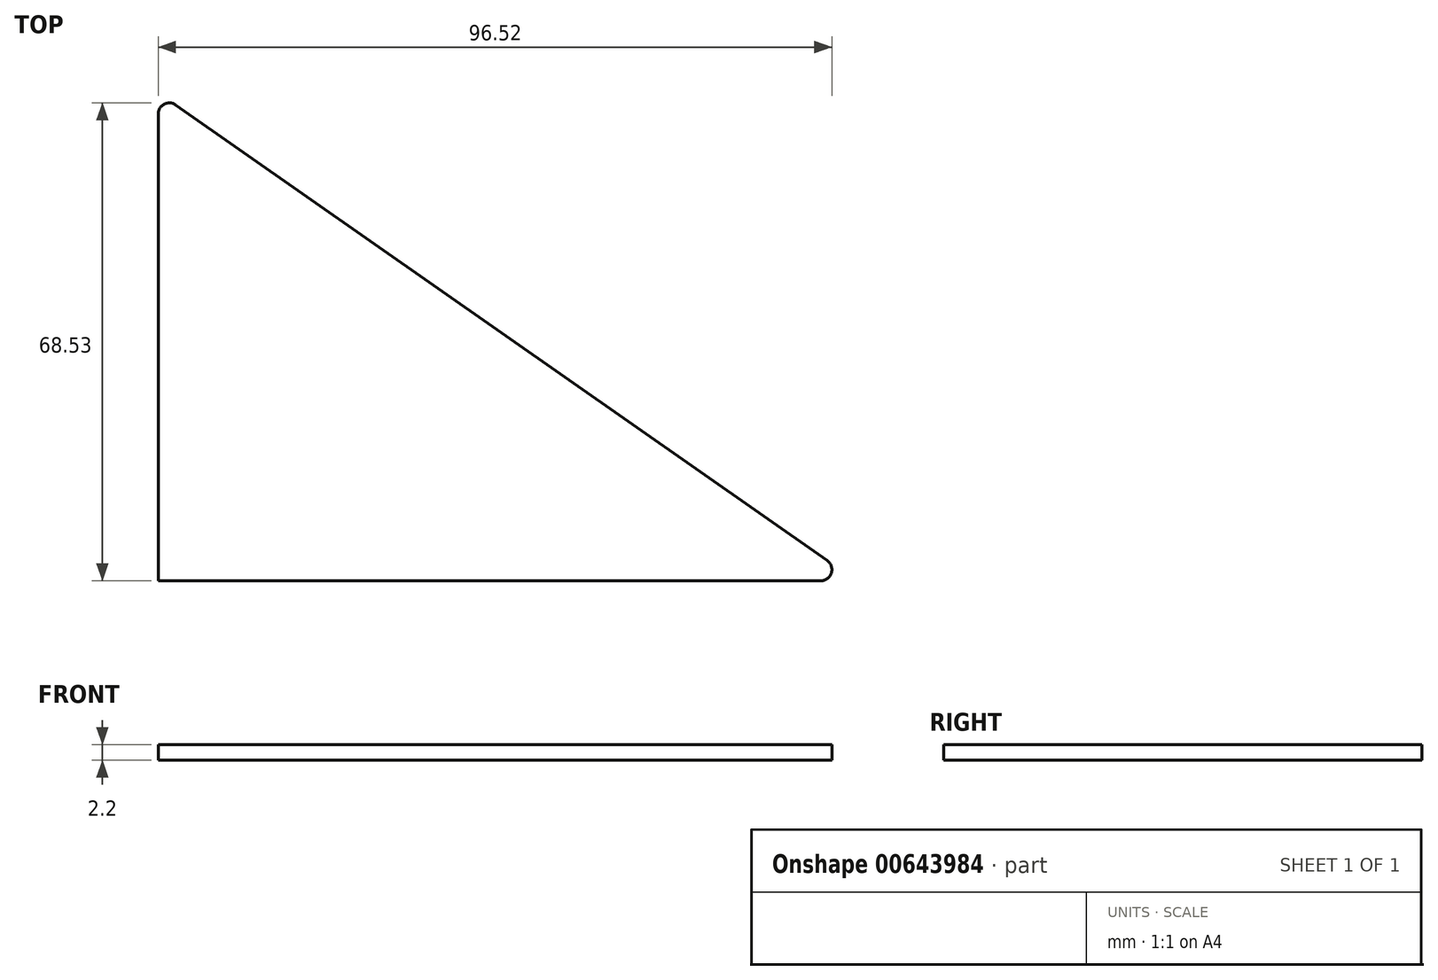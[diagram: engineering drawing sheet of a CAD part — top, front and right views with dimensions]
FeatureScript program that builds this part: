
annotation { "Feature Type Name" : "Feature", "Feature Type Description" : "" }
export const myFeature = defineFeature(function(context is Context, id is Id, definition is map)
    precondition{}
    {
        {
            var Q0;
            Q0=qCreatedBy(makeId("Top.planeOp"),FACE);
            var sketch = newSketch(context, id + "F0", { "sketchPlane" : qUnion([Q0])});
            skLineSegment(sketch, "E0", {"start": v(0, 0) * mm, "end": v(0, 70) * mm});
            skLineSegment(sketch, "E1", {"start": v(0, 0) * mm, "end": v(100, 0) * mm});
            skLineSegment(sketch, "E2", {"start": v(100, 0) * mm, "end": v(0, 70) * mm});
            skSolve(sketch);
        }
        {
            var Q0;
            Q0=makeQuery(id+"F0.imprint","IMPRINT",FACE,{"disambiguationData":[TD([[makeQuery(id+"F0.imprint","IMPRINT",EDGE,{"derivedFrom":sQuery(id+"F0.wireOp",EDGE,"E0")}),-1.0]])]});
            extrude(context, id + "F1", {"entities" : qUnion([Q0]), "depth" : 2.2 * mm, "offsetDistance" : 25 * mm});
        }
        {
            var Q0;
            Q0=makeQuery(id+"F1.opExtrude","SWEPT_EDGE",EDGE,{"disambiguationData":[OSD([sQuery(id+"F0.wireOp",EDGE,"E1"),sQuery(id+"F0.wireOp",EDGE,"E2")])]});
            var Q1;
            Q1=makeQuery(id+"F1.opExtrude","SWEPT_EDGE",EDGE,{"disambiguationData":[OSD([sQuery(id+"F0.wireOp",EDGE,"E0"),sQuery(id+"F0.wireOp",EDGE,"E2")])]});
            fillet(context, id + "F2", {"entities" : qUnion([Q0, Q1]), "radius" : 1.6 * mm, "tangentPropagation" : true, "allowEdgeOverflow" : false});
        }
    });
